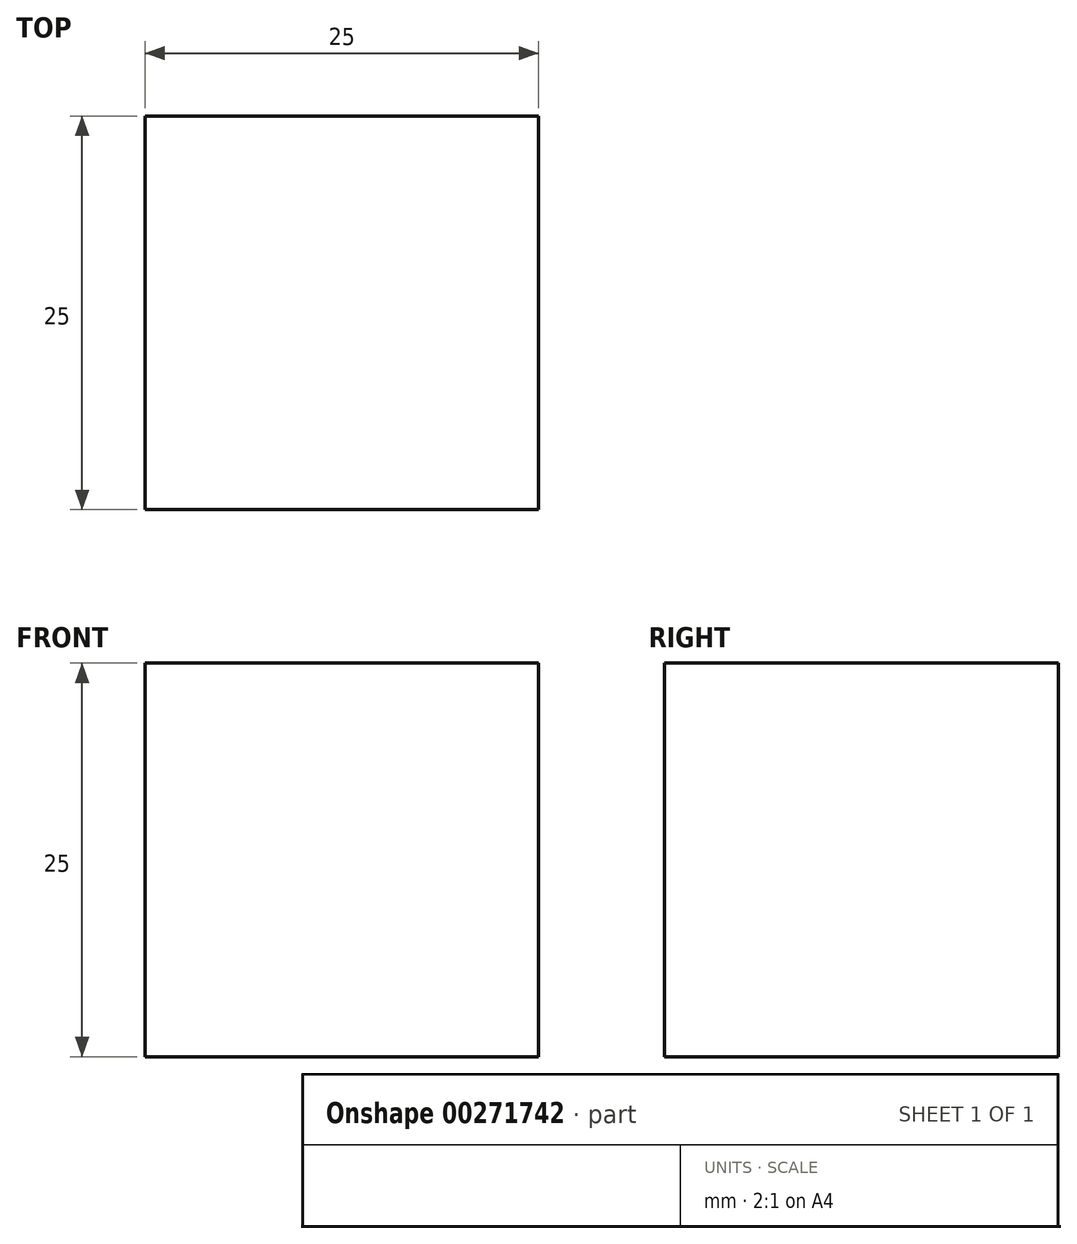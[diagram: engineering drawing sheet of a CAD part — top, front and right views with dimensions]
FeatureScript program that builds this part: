
annotation { "Feature Type Name" : "Feature", "Feature Type Description" : "" }
export const myFeature = defineFeature(function(context is Context, id is Id, definition is map)
    precondition{}
    {
        {
            var Q0;
            Q0=qCreatedBy(makeId("Top.planeOp"),FACE);
            var sketch = newSketch(context, id + "F0", { "sketchPlane" : qUnion([Q0])});
            skLineSegment(sketch, "E0.bottom", {"start": v(12.5, -12.5) * mm, "end": v(-12.5, -12.5) * mm});
            skLineSegment(sketch, "E0.top", {"start": v(12.5, 12.5) * mm, "end": v(-12.5, 12.5) * mm});
            skLineSegment(sketch, "E0.left", {"start": v(12.5, -12.5) * mm, "end": v(12.5, 12.5) * mm});
            skLineSegment(sketch, "E0.right", {"start": v(-12.5, -12.5) * mm, "end": v(-12.5, 12.5) * mm});
            skPoint(sketch, "E0.middle", {"position": v(0, 0) * mm});
            skSolve(sketch);
        }
        {
            var Q0;
            Q0 = qSketchRegion(id + "F0", true);
            extrude(context, id + "F1", {"entities" : qUnion([Q0]), "depth" : 25 * mm, "offsetDistance" : 25 * mm});
        }
    });
